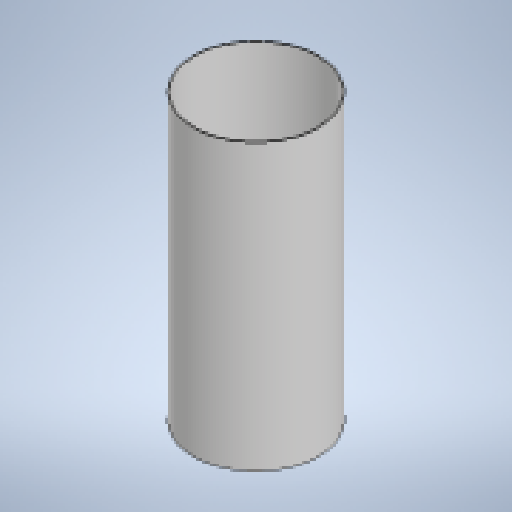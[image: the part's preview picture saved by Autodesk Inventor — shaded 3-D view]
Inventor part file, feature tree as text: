
AUTODESK INVENTOR PART (.ipt)
format: ipt  version: 2025 (Build 290162010, 162A)  size: 133,120 bytes
history: native  units: mm
features: extrude x1, shell x1, sketch x1
ambient origin geometry x8: Origin, YZ Plane, XZ Plane, XY Plane, X Axis, Y Axis, Z Axis, Center Point
bodies: Solid1 (feature_tree)
feature tree (3):
  extrude  "Extrusion1"  Depth=2500.0mm TaperAngle=0.0deg
  shell  "Shell1"  Thickness=10.0mm
  sketch  "Sketch1"  dims[d0=1100.0mm d1=2500.0mm d2=0.0mm d3=10.0mm]
